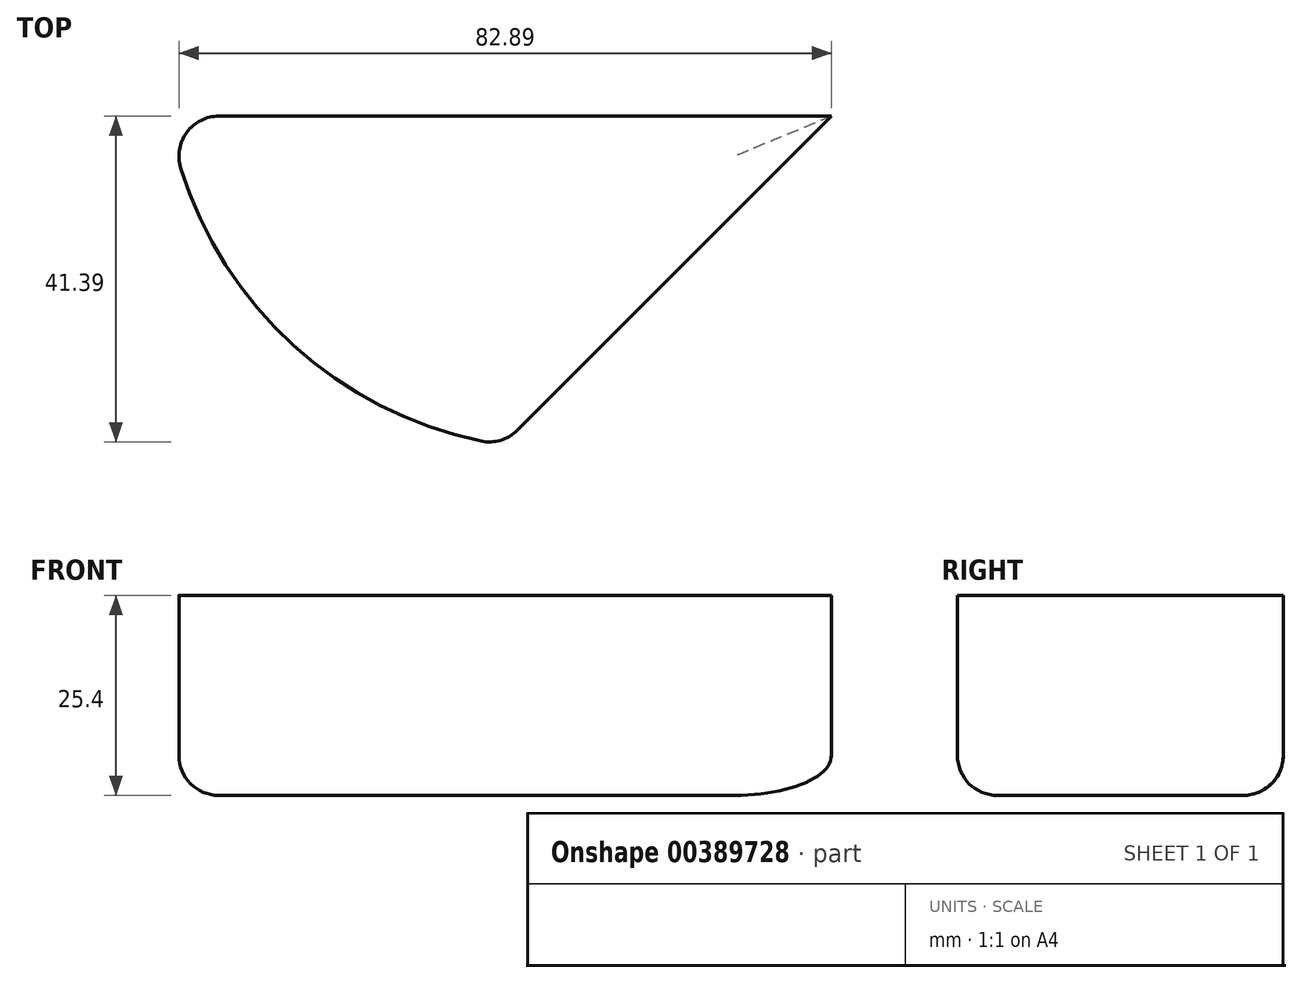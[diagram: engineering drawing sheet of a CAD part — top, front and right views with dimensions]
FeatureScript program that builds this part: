
annotation { "Feature Type Name" : "Feature", "Feature Type Description" : "" }
export const myFeature = defineFeature(function(context is Context, id is Id, definition is map)
    precondition{}
    {
        {
            var Q0;
            Q0=qCreatedBy(makeId("Top.planeOp"),FACE);
            var sketch = newSketch(context, id + "F0", { "sketchPlane" : qUnion([Q0])});
            skLineSegment(sketch, "E0.bottom", {"start": v(-108.87, -15.02) * mm, "end": v(9.2, -15.02) * mm});
            skLineSegment(sketch, "E0.top", {"start": v(-108.87, -57.37) * mm, "end": v(9.2, -57.37) * mm});
            skLineSegment(sketch, "E0.left", {"start": v(-108.87, -15.02) * mm, "end": v(-108.87, -57.37) * mm});
            skLineSegment(sketch, "E0.right", {"start": v(9.2, -15.02) * mm, "end": v(9.2, -57.37) * mm});
            skSolve(sketch);
        }
        {
            var Q0;
            Q0=makeQuery(id+"F0.imprint","IMPRINT",FACE,{"disambiguationData":[TD([[makeQuery(id+"F0.imprint","IMPRINT",EDGE,{"derivedFrom":sQuery(id+"F0.wireOp",EDGE,"E0.bottom")}),-1.0]])]});
            extrude(context, id + "F1", {"entities" : qUnion([Q0]), "depth" : 25.4 * mm});
        }
        {
            var Q0;
            Q0=makeQuery(id+"F1.opExtrude","SWEPT_EDGE",EDGE,{"disambiguationData":[OSD([sQuery(id+"F0.wireOp",EDGE,"E0.top"),sQuery(id+"F0.wireOp",EDGE,"E0.left")])]});
            fillet(context, id + "F2", {"entities" : qUnion([Q0]), "radius" : 50.8 * mm, "tangentPropagation" : true, "allowEdgeOverflow" : false});
        }
        {
            var Q0;
            Q0=makeQuery(id+"F1.opExtrude","SWEPT_EDGE",EDGE,{"disambiguationData":[OSD([sQuery(id+"F0.wireOp",EDGE,"E0.top"),sQuery(id+"F0.wireOp",EDGE,"E0.right")])]});
            chamfer(context, id + "F3", {"entities" : qUnion([Q0]), "width" : 76.2 * mm, "tangentPropagation" : true});
        }
        {
            var Q0;
            {var subQ0=sQuery(id+"F0.wireOp",EDGE,"E0.top");Q0=makeQuery(id+"F3.opChamfer","BLEND_EDGE",EDGE,{"blendedFrom":[makeQuery(id+"F1.opExtrude","SWEPT_EDGE",EDGE,{"disambiguationData":[OSD([subQ0,sQuery(id+"F0.wireOp",EDGE,"E0.right")])]}),makeQuery(id+"F2.opFillet","BLEND_FACE",FACE,{"disambiguationData":[OSD([subQ0,sQuery(id+"F0.wireOp",EDGE,"E0.left")])]})],"blendedInto":[makeQuery(id+"F2.opFillet","BLEND_FACE",FACE,{"disambiguationData":[OSD([subQ0,sQuery(id+"F0.wireOp",EDGE,"E0.left")])]})]});}
            fillet(context, id + "F4", {"entities" : qUnion([Q0]), "radius" : 5.08 * mm, "tangentPropagation" : true, "allowEdgeOverflow" : false});
        }
        {
            var Q0;
            Q0=makeQuery(id+"F2.opFillet","BLEND_EDGE",EDGE,{"blendedFrom":[makeQuery(id+"F1.opExtrude","SWEPT_EDGE",EDGE,{"disambiguationData":[OSD([sQuery(id+"F0.wireOp",EDGE,"E0.top"),sQuery(id+"F0.wireOp",EDGE,"E0.left")])]}),makeQuery(id+"F1.opExtrude","SWEPT_FACE",FACE,{"disambiguationData":[OSD([sQuery(id+"F0.wireOp",EDGE,"E0.bottom")])]})],"blendedInto":[makeQuery(id+"F1.opExtrude","SWEPT_FACE",FACE,{"disambiguationData":[OSD([sQuery(id+"F0.wireOp",EDGE,"E0.bottom")])]})]});
            fillet(context, id + "F5", {"entities" : qUnion([Q0]), "radius" : 5.08 * mm, "tangentPropagation" : true, "allowEdgeOverflow" : false});
        }
        {
            var Q0;
            {var subQ0=sQuery(id+"F0.wireOp",EDGE,"E0.right");var subQ1=sQuery(id+"F0.wireOp",EDGE,"E0.top");Q0=makeQuery(id+"F3.opChamfer","BLEND_EDGE",EDGE,{"blendedFrom":[makeQuery(id+"F1.opExtrude","SWEPT_EDGE",EDGE,{"disambiguationData":[OSD([subQ1,subQ0])]}),makeQuery(id+"F1.opExtrude","CAP_FACE",FACE,{"disambiguationData":[OSD([sQuery(id+"F0.wireOp",EDGE,"E0.bottom"),subQ1,sQuery(id+"F0.wireOp",EDGE,"E0.left"),subQ0])],"isStart":true})],"blendedInto":[makeQuery(id+"F1.opExtrude","CAP_FACE",FACE,{"disambiguationData":[OSD([sQuery(id+"F0.wireOp",EDGE,"E0.bottom"),subQ1,sQuery(id+"F0.wireOp",EDGE,"E0.left"),subQ0])],"isStart":true})]});}
            fillet(context, id + "F6", {"entities" : qUnion([Q0]), "radius" : 5.08 * mm, "tangentPropagation" : true, "allowEdgeOverflow" : false});
        }
    });
